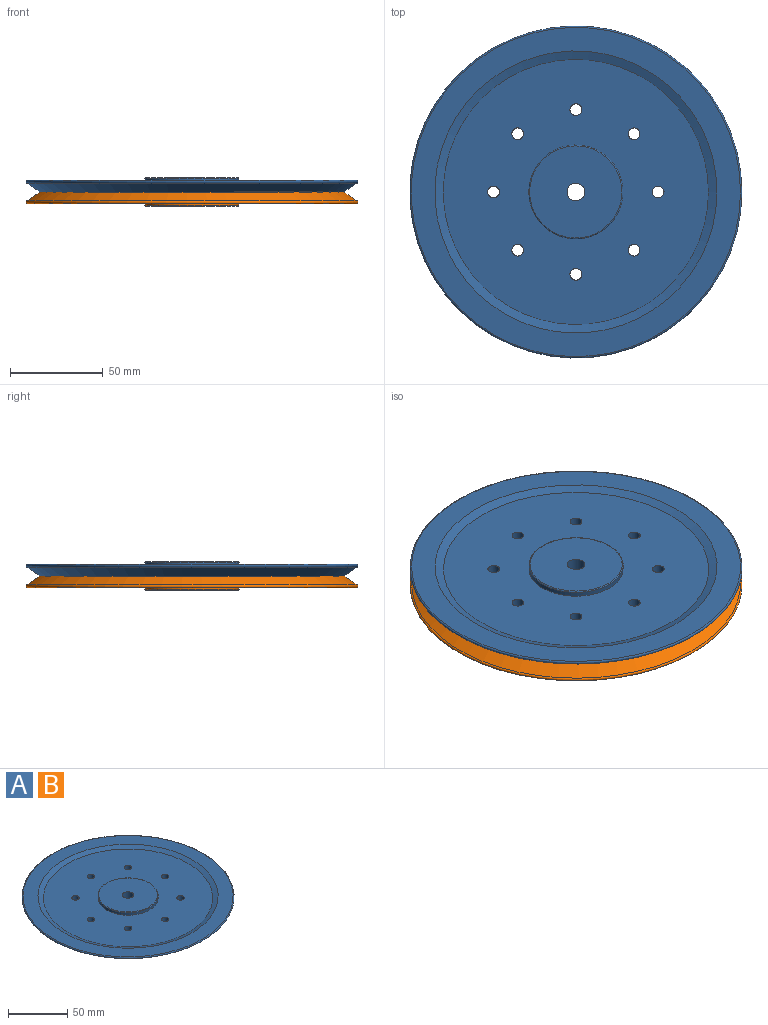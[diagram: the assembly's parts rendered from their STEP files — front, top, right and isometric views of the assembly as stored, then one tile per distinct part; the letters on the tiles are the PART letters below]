
ASSEMBLY  parts=2 mates=1
PART A: 18 faces, bbox 194.2x194.2x7.6 mm
  f0: torus R=24.89mm, axis (0,0,1), area 127.4mm2, adj f1,f9
  f1: plane 49.78x49.78mm, normal (0,0,1), area 1874.7mm2, adj f0,f2
  f2: cylinder r=4.76mm len=9.53mm, axis (0,0,1), area 228mm2, adj f1,f3
  f3: plane 164.2x164.2mm, normal (0,0,-1), area 20850.2mm2, adj f2,f4,f10,f11,f12,f13,f14,f15
  f4: cone r=88.9mm half-angle=55deg, axis (0,0,1), area 4460.5mm2, adj f3,f5
  f5: torus R=88.9mm, axis (0,0,1), area 1400.8mm2, adj f4,f6
  f6: plane 177.8x177.8mm, normal (0,0,1), area 6587.2mm2, adj f5,f7
  f7: cone r=76.2mm half-angle=68.7deg, axis (0,0,1), area 2279.4mm2, adj f6,f8
  f8: plane 143.25x143.25mm, normal (0,0,1), area 13836.9mm2, adj f7,f9,f10,f11,f12,f13,f14,f15
  f9: cylinder r=25.4mm len=50.8mm, axis (0,0,1), area 404.9mm2, adj f0,f8
  f10: cylinder r=3.17mm len=6.35mm, axis (0,0,1), area 91.2mm2, adj f3,f8
  f11: cylinder r=3.17mm len=6.35mm, axis (0,0,1), area 91.2mm2, adj f3,f8
  f12: cylinder r=3.17mm len=6.35mm, axis (0,0,1), area 91.2mm2, adj f3,f8
  f13: cylinder r=3.17mm len=6.35mm, axis (0,0,1), area 91.2mm2, adj f3,f8
  f14: cylinder r=3.17mm len=6.35mm, axis (0,0,1), area 91.2mm2, adj f3,f8
  f15: cylinder r=3.17mm len=6.35mm, axis (0,0,1), area 91.2mm2, adj f3,f8
  f16: cylinder r=3.17mm len=6.35mm, axis (0,0,1), area 91.2mm2, adj f3,f8
  f17: cylinder r=3.17mm len=6.35mm, axis (0,0,1), area 91.2mm2, adj f3,f8
PART B: same geometry as A
PLACE A t=(-49.81,4.71,-39.48)mm
PLACE B rot(axis=(1,0,0),180deg) t=(-49.81,4.71,-39.48)mm
MATE fastened B.f7 <-> A.f7  axis (0,0,1) through (-49.81,4.71,-39.48)mm
